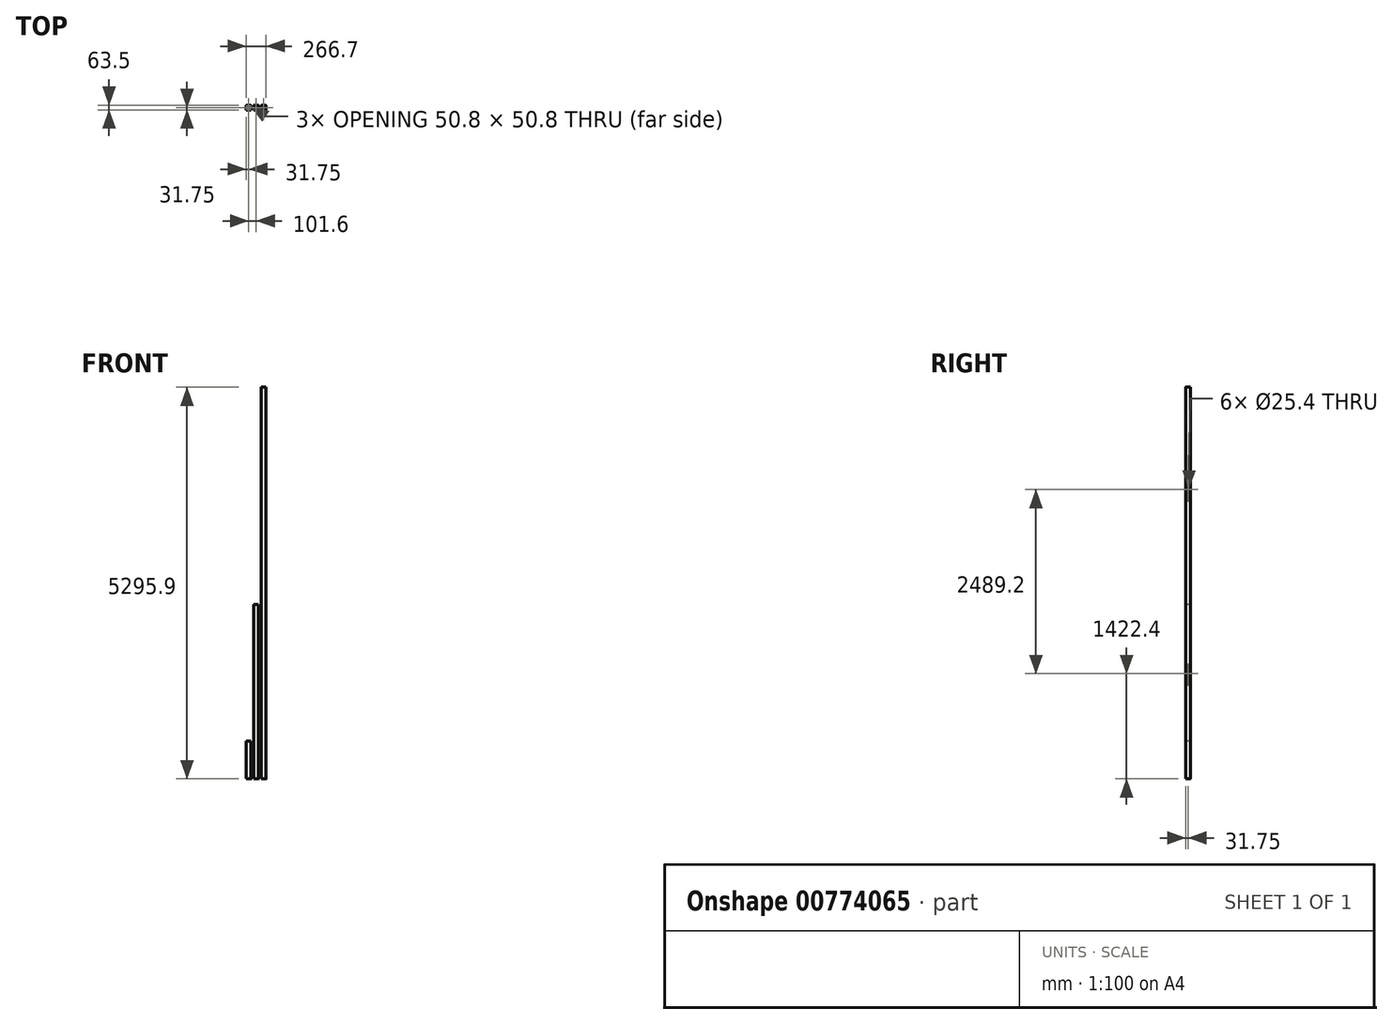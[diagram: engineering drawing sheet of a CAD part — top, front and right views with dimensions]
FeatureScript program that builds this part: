
annotation { "Feature Type Name" : "Feature", "Feature Type Description" : "" }
export const myFeature = defineFeature(function(context is Context, id is Id, definition is map)
    precondition{}
    {
        {
            var Q0;
            Q0=qCreatedBy(makeId("Top.planeOp"),FACE);
            var sketch = newSketch(context, id + "F0", { "sketchPlane" : qUnion([Q0])});
            skLineSegment(sketch, "E0.bottom", {"start": v(28.57, 31.75) * mm, "end": v(-28.58, 31.75) * mm});
            skLineSegment(sketch, "E0.top", {"start": v(28.57, -31.75) * mm, "end": v(-28.58, -31.75) * mm});
            skLineSegment(sketch, "E0.left", {"start": v(31.75, 28.58) * mm, "end": v(31.75, -28.57) * mm});
            skLineSegment(sketch, "E0.right", {"start": v(-31.75, 28.58) * mm, "end": v(-31.75, -28.57) * mm});
            skPoint(sketch, "E0.middle", {"position": v(0, 0) * mm});
            skLineSegment(sketch, "E1.bottom", {"start": v(22.22, 25.4) * mm, "end": v(-22.23, 25.4) * mm});
            skLineSegment(sketch, "E1.top", {"start": v(22.22, -25.4) * mm, "end": v(-22.23, -25.4) * mm});
            skLineSegment(sketch, "E1.left", {"start": v(25.4, 22.23) * mm, "end": v(25.4, -22.22) * mm});
            skLineSegment(sketch, "E1.right", {"start": v(-25.4, 22.23) * mm, "end": v(-25.4, -22.23) * mm});
            skPoint(sketch, "E2.visualSharp", {"position": v(-31.75, 31.75) * mm});
            skArc(sketch, "E2.filletArc", {"start": v(-28.58, 31.75) * mm, "mid": v(-30.82, 30.82) * mm, "end": v(-31.75, 28.58) * mm});
            skPoint(sketch, "E3.visualSharp", {"position": v(-25.4, 25.4) * mm});
            skArc(sketch, "E3.filletArc", {"start": v(-22.23, 25.4) * mm, "mid": v(-24.47, 24.47) * mm, "end": v(-25.4, 22.23) * mm});
            skPoint(sketch, "E4.visualSharp", {"position": v(25.4, 25.4) * mm});
            skArc(sketch, "E4.filletArc", {"start": v(25.4, 22.23) * mm, "mid": v(24.47, 24.47) * mm, "end": v(22.22, 25.4) * mm});
            skPoint(sketch, "E5.visualSharp", {"position": v(31.75, 31.75) * mm});
            skArc(sketch, "E5.filletArc", {"start": v(31.75, 28.58) * mm, "mid": v(30.82, 30.82) * mm, "end": v(28.57, 31.75) * mm});
            skPoint(sketch, "E6.visualSharp", {"position": v(25.4, -25.4) * mm});
            skArc(sketch, "E6.filletArc", {"start": v(22.22, -25.4) * mm, "mid": v(24.47, -24.47) * mm, "end": v(25.4, -22.22) * mm});
            skPoint(sketch, "E7.visualSharp", {"position": v(31.75, -31.75) * mm});
            skArc(sketch, "E7.filletArc", {"start": v(28.57, -31.75) * mm, "mid": v(30.82, -30.82) * mm, "end": v(31.75, -28.57) * mm});
            skPoint(sketch, "E8.visualSharp", {"position": v(-31.75, -31.75) * mm});
            skArc(sketch, "E8.filletArc", {"start": v(-31.75, -28.57) * mm, "mid": v(-30.82, -30.82) * mm, "end": v(-28.58, -31.75) * mm});
            skPoint(sketch, "E9.visualSharp", {"position": v(-25.4, -25.4) * mm});
            skArc(sketch, "E9.filletArc", {"start": v(-25.4, -22.23) * mm, "mid": v(-24.47, -24.47) * mm, "end": v(-22.23, -25.4) * mm});
            skPoint(sketch, "E10.1.0.0", {"position": v(133.35, 31.75) * mm});
            skPoint(sketch, "E10.1.0.1", {"position": v(76.2, 25.4) * mm});
            skPoint(sketch, "E10.1.0.2", {"position": v(69.85, 31.75) * mm});
            skPoint(sketch, "E10.1.0.3", {"position": v(101.6, 0) * mm});
            skPoint(sketch, "E10.1.0.4", {"position": v(127, -25.4) * mm});
            skPoint(sketch, "E10.1.0.5", {"position": v(69.85, -31.75) * mm});
            skPoint(sketch, "E10.1.0.6", {"position": v(76.2, -25.4) * mm});
            skLineSegment(sketch, "E10.1.0.7", {"start": v(130.18, -31.75) * mm, "end": v(73.03, -31.75) * mm});
            skLineSegment(sketch, "E10.1.0.8", {"start": v(133.35, 28.57) * mm, "end": v(133.35, -28.57) * mm});
            skLineSegment(sketch, "E10.1.0.9", {"start": v(123.83, 25.4) * mm, "end": v(79.38, 25.4) * mm});
            skLineSegment(sketch, "E10.1.0.10", {"start": v(76.2, 22.23) * mm, "end": v(76.2, -22.23) * mm});
            skLineSegment(sketch, "E10.1.0.11", {"start": v(123.83, -25.4) * mm, "end": v(79.38, -25.4) * mm});
            skPoint(sketch, "E10.1.0.12", {"position": v(127, 25.4) * mm});
            skLineSegment(sketch, "E10.1.0.13", {"start": v(127, 22.22) * mm, "end": v(127, -22.22) * mm});
            skLineSegment(sketch, "E10.1.0.14", {"start": v(69.85, 28.57) * mm, "end": v(69.85, -28.57) * mm});
            skLineSegment(sketch, "E10.1.0.15", {"start": v(130.18, 31.75) * mm, "end": v(73.03, 31.75) * mm});
            skPoint(sketch, "E10.1.0.16", {"position": v(133.35, -31.75) * mm});
            skPoint(sketch, "E10.1.0.17", {"position": v(101.6, 0) * mm});
            skArc(sketch, "E10.1.0.18", {"start": v(69.85, -28.57) * mm, "mid": v(70.78, -30.82) * mm, "end": v(73.03, -31.75) * mm});
            skArc(sketch, "E10.1.0.19", {"start": v(76.2, -22.23) * mm, "mid": v(77.13, -24.47) * mm, "end": v(79.38, -25.4) * mm});
            skArc(sketch, "E10.1.0.20", {"start": v(130.18, -31.75) * mm, "mid": v(132.42, -30.82) * mm, "end": v(133.35, -28.57) * mm});
            skArc(sketch, "E10.1.0.21", {"start": v(123.83, -25.4) * mm, "mid": v(126.07, -24.47) * mm, "end": v(127, -22.22) * mm});
            skArc(sketch, "E10.1.0.22", {"start": v(133.35, 28.57) * mm, "mid": v(132.42, 30.82) * mm, "end": v(130.18, 31.75) * mm});
            skArc(sketch, "E10.1.0.23", {"start": v(79.38, 25.4) * mm, "mid": v(77.13, 24.47) * mm, "end": v(76.2, 22.23) * mm});
            skArc(sketch, "E10.1.0.24", {"start": v(73.03, 31.75) * mm, "mid": v(70.78, 30.82) * mm, "end": v(69.85, 28.57) * mm});
            skArc(sketch, "E10.1.0.25", {"start": v(127, 22.22) * mm, "mid": v(126.07, 24.47) * mm, "end": v(123.83, 25.4) * mm});
            skPoint(sketch, "E10.2.0.0", {"position": v(234.95, 31.75) * mm});
            skPoint(sketch, "E10.2.0.1", {"position": v(177.8, 25.4) * mm});
            skPoint(sketch, "E10.2.0.2", {"position": v(171.45, 31.75) * mm});
            skPoint(sketch, "E10.2.0.3", {"position": v(203.2, 0) * mm});
            skPoint(sketch, "E10.2.0.4", {"position": v(228.6, -25.4) * mm});
            skPoint(sketch, "E10.2.0.5", {"position": v(171.45, -31.75) * mm});
            skPoint(sketch, "E10.2.0.6", {"position": v(177.8, -25.4) * mm});
            skLineSegment(sketch, "E10.2.0.7", {"start": v(231.78, -31.75) * mm, "end": v(174.63, -31.75) * mm});
            skLineSegment(sketch, "E10.2.0.8", {"start": v(234.95, 28.57) * mm, "end": v(234.95, -28.57) * mm});
            skLineSegment(sketch, "E10.2.0.9", {"start": v(225.43, 25.4) * mm, "end": v(180.98, 25.4) * mm});
            skLineSegment(sketch, "E10.2.0.10", {"start": v(177.8, 22.23) * mm, "end": v(177.8, -22.23) * mm});
            skLineSegment(sketch, "E10.2.0.11", {"start": v(225.43, -25.4) * mm, "end": v(180.98, -25.4) * mm});
            skPoint(sketch, "E10.2.0.12", {"position": v(228.6, 25.4) * mm});
            skLineSegment(sketch, "E10.2.0.13", {"start": v(228.6, 22.22) * mm, "end": v(228.6, -22.22) * mm});
            skLineSegment(sketch, "E10.2.0.14", {"start": v(171.45, 28.57) * mm, "end": v(171.45, -28.57) * mm});
            skLineSegment(sketch, "E10.2.0.15", {"start": v(231.78, 31.75) * mm, "end": v(174.63, 31.75) * mm});
            skPoint(sketch, "E10.2.0.16", {"position": v(234.95, -31.75) * mm});
            skPoint(sketch, "E10.2.0.17", {"position": v(203.2, 0) * mm});
            skArc(sketch, "E10.2.0.18", {"start": v(171.45, -28.57) * mm, "mid": v(172.38, -30.82) * mm, "end": v(174.63, -31.75) * mm});
            skArc(sketch, "E10.2.0.19", {"start": v(177.8, -22.23) * mm, "mid": v(178.73, -24.47) * mm, "end": v(180.98, -25.4) * mm});
            skArc(sketch, "E10.2.0.20", {"start": v(231.78, -31.75) * mm, "mid": v(234.02, -30.82) * mm, "end": v(234.95, -28.57) * mm});
            skArc(sketch, "E10.2.0.21", {"start": v(225.43, -25.4) * mm, "mid": v(227.67, -24.47) * mm, "end": v(228.6, -22.22) * mm});
            skArc(sketch, "E10.2.0.22", {"start": v(234.95, 28.57) * mm, "mid": v(234.02, 30.82) * mm, "end": v(231.78, 31.75) * mm});
            skArc(sketch, "E10.2.0.23", {"start": v(180.98, 25.4) * mm, "mid": v(178.73, 24.47) * mm, "end": v(177.8, 22.23) * mm});
            skArc(sketch, "E10.2.0.24", {"start": v(174.63, 31.75) * mm, "mid": v(172.38, 30.82) * mm, "end": v(171.45, 28.57) * mm});
            skArc(sketch, "E10.2.0.25", {"start": v(228.6, 22.22) * mm, "mid": v(227.67, 24.47) * mm, "end": v(225.43, 25.4) * mm});
            skLineSegment(sketch, "E10.direction1", {"start": v(-31.75, -31.75) * mm, "end": v(69.85, -31.75) * mm, "construction": true});
            skSolve(sketch);
        }
        {
            var Q0;
            Q0=makeQuery(id+"F0.imprint","IMPRINT",FACE,{"disambiguationData":[TD([[makeQuery(id+"F0.imprint","IMPRINT",EDGE,{"derivedFrom":sQuery(id+"F0.wireOp",EDGE,"E0.bottom")}),1.0]])]});
            extrude(context, id + "F1", {"entities" : qUnion([Q0]), "depth" : 508 * mm, "offsetDistance" : 25.4 * mm});
        }
        {
            var Q0;
            Q0=makeQuery(id+"F0.imprint","IMPRINT",FACE,{"disambiguationData":[TD([[makeQuery(id+"F0.imprint","IMPRINT",EDGE,{"derivedFrom":sQuery(id+"F0.wireOp",EDGE,"E10.1.0.7")}),-1.0]])]});
            extrude(context, id + "F2", {"entities" : qUnion([Q0]), "operationType" : NewBodyOperationType.ADD, "depth" : 2355.85 * mm, "offsetDistance" : 25.4 * mm});
        }
        {
            var Q0;
            Q0=makeQuery(id+"F0.imprint","IMPRINT",FACE,{"disambiguationData":[TD([[makeQuery(id+"F0.imprint","IMPRINT",EDGE,{"derivedFrom":sQuery(id+"F0.wireOp",EDGE,"E10.2.0.7")}),-1.0]])]});
            extrude(context, id + "F3", {"entities" : qUnion([Q0]), "depth" : 5295.9 * mm, "offsetDistance" : 25.4 * mm});
        }
        {
            var Q0;
            Q0=makeQuery(id+"F2.opExtrude","SWEPT_FACE",FACE,{"disambiguationData":[OSD([sQuery(id+"F0.wireOp",EDGE,"E10.1.0.7")])]});
            var sketch = newSketch(context, id + "F4", { "sketchPlane" : qUnion([Q0])});
            skCircle(sketch, "E11", {"center": v(101.6, 2324.1) * mm, "radius": 12.7 * mm});
            skPoint(sketch, "E11.centerSnap0", {"position": v(101.6, 2355.85) * mm});
            skLineSegment(sketch, "E12.bottom", {"start": v(76.2, 2349.5) * mm, "end": v(127, 2349.5) * mm, "construction": true});
            skLineSegment(sketch, "E12.top", {"start": v(76.2, 2298.7) * mm, "end": v(127, 2298.7) * mm, "construction": true});
            skLineSegment(sketch, "E12.left", {"start": v(76.2, 2349.5) * mm, "end": v(76.2, 2298.7) * mm, "construction": true});
            skLineSegment(sketch, "E12.right", {"start": v(127, 2349.5) * mm, "end": v(127, 2298.7) * mm, "construction": true});
            skCircle(sketch, "E13", {"center": v(101.6, 31.75) * mm, "radius": 12.7 * mm});
            skLineSegment(sketch, "E14.bottom", {"start": v(76.2, 57.15) * mm, "end": v(127, 57.15) * mm, "construction": true});
            skLineSegment(sketch, "E14.top", {"start": v(76.2, 6.35) * mm, "end": v(127, 6.35) * mm, "construction": true});
            skLineSegment(sketch, "E14.left", {"start": v(76.2, 57.15) * mm, "end": v(76.2, 6.35) * mm, "construction": true});
            skLineSegment(sketch, "E14.right", {"start": v(127, 57.15) * mm, "end": v(127, 6.35) * mm, "construction": true});
            skLineSegment(sketch, "E15", {"start": v(101.6, 31.75) * mm, "end": v(101.6, 0) * mm, "construction": true});
            skLineSegment(sketch, "E16", {"start": v(101.6, 2324.1) * mm, "end": v(101.6, 2355.85) * mm, "construction": true});
            skSolve(sketch);
        }
        {
            var Q0;
            Q0=makeQuery(id+"F1.opExtrude","SWEPT_FACE",FACE,{"disambiguationData":[OSD([sQuery(id+"F0.wireOp",EDGE,"E0.right")])]});
            var sketch = newSketch(context, id + "F5", { "sketchPlane" : qUnion([Q0])});
            skLineSegment(sketch, "E17", {"start": v(0, 508) * mm, "end": v(0, 0) * mm, "construction": true});
            skCircle(sketch, "E18", {"center": v(0, 241.3) * mm, "radius": 8.73 * mm});
            skCircle(sketch, "E19", {"center": v(0, 165.1) * mm, "radius": 8.73 * mm});
            skCircle(sketch, "E20", {"center": v(0, 149.23) * mm, "radius": 8.73 * mm, "construction": true});
            skCircle(sketch, "E21", {"center": v(0, 73.03) * mm, "radius": 8.73 * mm, "construction": true});
            skSolve(sketch);
        }
        {
            var Q0;
            Q0=makeQuery(id+"F3.opExtrude","SWEPT_FACE",FACE,{"disambiguationData":[OSD([sQuery(id+"F0.wireOp",EDGE,"E10.2.0.8")])]});
            var sketch = newSketch(context, id + "F6", { "sketchPlane" : qUnion([Q0])});
            skCircle(sketch, "E22", {"center": v(0, 3911.6) * mm, "radius": 12.7 * mm});
            skPoint(sketch, "E22.centerSnap0", {"position": v(0, 5295.9) * mm});
            skCircle(sketch, "E23", {"center": v(0, 1422.4) * mm, "radius": 12.7 * mm});
            skPoint(sketch, "E23.centerSnap0", {"position": v(0, 0) * mm});
            skSolve(sketch);
        }
        {
            var Q0;
            Q0 = qSketchRegion(id + "F6", true);
            extrude(context, id + "F7", {"entities" : qUnion([Q0]), "operationType" : NewBodyOperationType.REMOVE, "endBound" : BoundingType.THROUGH_ALL, "oppositeDirection" : true, "depth" : 25.4 * mm, "offsetDistance" : 25.4 * mm});
        }
    });
